# Revit family: ASH_ArmitageShanks_CounterTopWashBasins_Orbit21-55cm
name_source: partatom
category: Plumbing Fixtures
revit_build: Autodesk Revit MEP 2012 (Build: 20110309_2315(x64)
units: mm (PartAtom-declared; Revit-internal decimal feet)

## types (7) — shared parameters
Accessories = www.idealspec.co.uk
AreaUnits = millimeters
Assembly Code = C1030200
AssetType = Fixed
BasinMaterial = ASH_ArmitageShanks _Sanitaryware_White4_Render
Brand = Armitage Shanks
Category = SanitaryTerminal_WASHHANDBASIN_UK
Color = White
ConnectionType = Plumbing
Default Elevation = 1219 mm
DrainSize = 32 mm  [stored 0.104987 ft]
DurationUnit = year
ECA = No
ExpectedLife = 30
Finish = White
IfcExportAs = IfcSanitaryTerminalType
IfcExportType = WASHHANDBASIN
InstallationInstructions = www.idealspec.co.uk/resources.html
LinearUnits = millimeters
ManufacturerURL = www.idealspec.co.uk
Material = Vitreous china
NBSDescription = Counter top wash basins
NBSReference = 35-70-70/360
NettWeight = 9.1 Kg
NominalDepth = 460 mm
NominalHeight = 188 mm
NominalLength = 460 mm
NominalWidth = 550 mm
Shape = Eliptical
Size = 550 x 460 x 190 mm
Space = Internal
SpareParts = www.fastpart-spares.co.uk
URL = www.idealspec.co.uk
Uniclass2 = Pr_40_20_96_18
Version = 1
VolumeUnits = Litres
WRAS = No
WarrantyDescription = Manufacturers warranty
WarrantyDurationParts = 99
WarrantyDurationUnit = year
WashHandBasinType = HANDRINSE
WaterEfficientProduct = No
zero-valued in all types: CWFU, HWFU, WFU

## per-type parameters (varying)
| type | BIMObjectName | CTH | Description | Features | LHTH | Model | ModelNumber | ModelReference | Name | ProductInformation | RHTH | WashHandBasinMounting |
| S248601 - orbit 21 55cm Countertop Washbasin 1 Taphole With overflow | ASH_ArmitageShanks_CounterTopWashBasins_Orbit21_S2486 | Yes | Orbit 21 55 cm countertop washbasin 1 taphole with overflow | 55 cm countertop washbasin 1 taphole with overflow | No | S248601 | S248601 | Orbit 21 55 cm countertop washbasin 1 taphole with overflow | CounterTopWashBasins_Orbit21_S2486_ArmitageShanks | www.idealspec.co.uk/assets/datasheet/S248601 | No | Wall hung |
| S248701 - orbit 21 55cm Countertop Washbasin, 1 Taphole no overflow | ASH_ArmitageShanks_CounterTopWashBasins_Orbit21_S2487 | Yes | Orbit 21 55 cm countertop washbasin, 1 taphole no overflow | 55 cm countertop washbasin, 1 taphole no overflow | No | S248701 | S248701 | Orbit 21 55 cm countertop washbasin, 1 taphole no overflow | CounterTopWashBasins_Orbit21_S2487_ArmitageShanks | www.idealspec.co.uk/assets/datasheet/S248701 | No | Wall hung |
| S248801 - orbit 21 55cm Countertop Washbasin 2 Taphole With overflow & chainhole | ASH_ArmitageShanks_CounterTopWashBasins_Orbit21_S2488 | No | Orbit 21 55 cm countertop washbasin 2 taphole with overflow & chainhole | 55 cm countertop washbasin 2 taphole with overflow & chainhole | Yes | S248801 | S248801 | Orbit 21 55 cm countertop washbasin 2 taphole with overflow & chainhole | CounterTopWashBasins_Orbit21_S2488_ArmitageShanks | www.idealspec.co.uk/resources.html | Yes | Wall hung |
| S248901 - orbit 21 55cm Countertop Washbasin, 2 Taphole no overflow, no chainhole | ASH_ArmitageShanks_CounterTopWashBasins_Orbit21_S2489 | No | Orbit 21 55 cm countertop washbasin, 2 taphole no overflow, no chainhole | 55 cm countertop washbasin, 2 taphole no overflow, no chainhole | Yes | S248901 | S248901 | Orbit 21 55 cm countertop washbasin, 2 taphole no overflow, no chainhole | CounterTopWashBasins_Orbit21_S2489_ArmitageShanks | www.idealspec.co.uk/assets/datasheet/S248901 | Yes | Wall hung |
| S249001 - orbit 21 55cm Countertop Washbasin, 1 RH Taphole no overflow, no chainhole | ASH_ArmitageShanks_CounterTopWashBasins_Orbit21_S2490 | No | Orbit 21 55 cm countertop washbasin, 1 rh taphole no overflow, no chainhole | 55 cm countertop washbasin, 1 rh taphole no overflow, no chainhole | No | S249001 | S249001 | Orbit 21 55 cm countertop washbasin, 1 rh taphole no overflow, no chainhole | CounterTopWashBasins_Orbit21_S2490_ArmitageShanks | www.idealspec.co.uk/assets/datasheet/S249001 | Yes | CounterTop |
| S249101 - orbit 21 55cm Countertop Washbasin 3 Taphole With overflow, no chainhole | ASH_ArmitageShanks_CounterTopWashBasins_Orbit21_S2491 | Yes | Orbit 21 55 cm countertop washbasin 3 taphole with overflow, no chainhole | 55 cm countertop washbasin 3 taphole with overflow, no chainhole | Yes | S249101 | S249101 | Orbit 21 55 cm countertop washbasin 3 taphole with overflow, no chainhole | CounterTopWashBasins_Orbit21_S2491_ArmitageShanks | www.idealspec.co.uk/assets/datasheet/S249101 | Yes | Wall hung |
| S251301 - orbit 21 55cm Countertop Washbasin 1 Taphole With overflow, no chainhole | ASH_ArmitageShanks_CounterTopWashBasins_Orbit21_S2513 | Yes | Orbit 21 55 cm countertop washbasin 1 taphole with overflow, no chainhole | 55 cm countertop washbasin 1 taphole with overflow, no chainhole | No | S251301 | S251301 | Orbit 21 55 cm countertop washbasin 1 taphole with overflow, no chainhole | CounterTopWashBasins_Orbit21_S2513_ArmitageShanks | www.idealspec.co.uk/assets/datasheet/S251301 | No | Wall hung |

note: [stored X ft] marks values corroborated as IEEE doubles in the binary element streams (Revit-internal decimal feet)

## geometry (parser evidence)
native form markers: Blend x3, Sweep x6
no freeform markers — native parametric forms only
